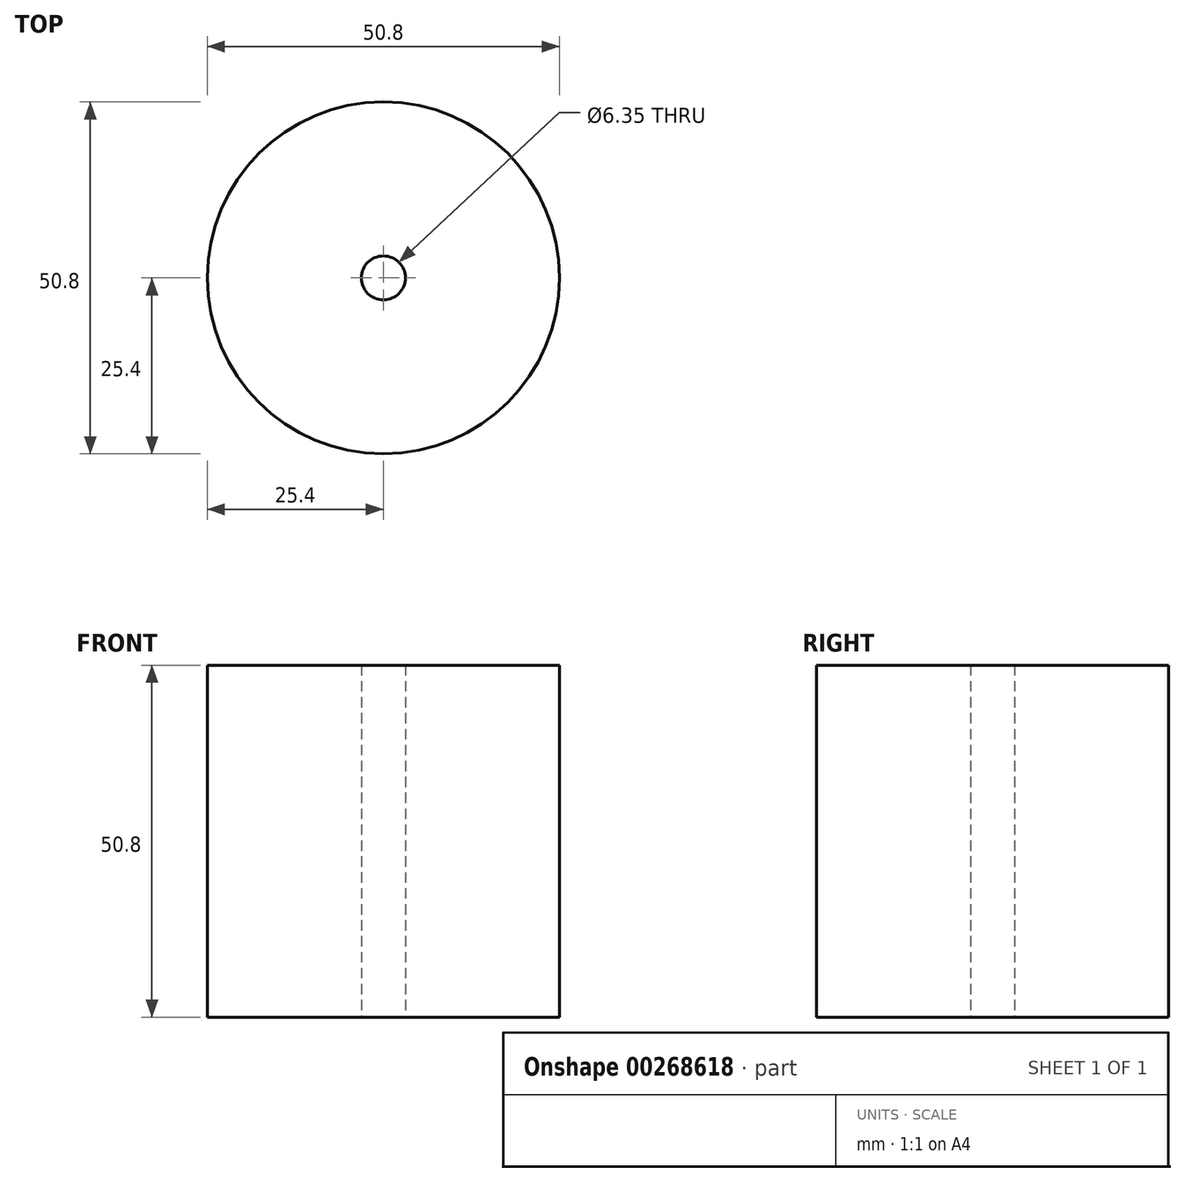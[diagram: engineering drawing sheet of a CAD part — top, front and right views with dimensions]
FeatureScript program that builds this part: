
annotation { "Feature Type Name" : "Feature", "Feature Type Description" : "" }
export const myFeature = defineFeature(function(context is Context, id is Id, definition is map)
    precondition{}
    {
        {
            var Q0;
            Q0=qCreatedBy(makeId("Top.planeOp"),FACE);
            var sketch = newSketch(context, id + "F0", { "sketchPlane" : qUnion([Q0])});
            skCircle(sketch, "E0", {"center": v(0, 0) * mm, "radius": 25.4 * mm});
            skCircle(sketch, "E1", {"center": v(0, 0) * mm, "radius": 3.17 * mm});
            skSolve(sketch);
        }
        {
            var Q0;
            Q0 = qSketchRegion(id + "F0", true);
            extrude(context, id + "F1", {"entities" : qUnion([Q0]), "depth" : 50.8 * mm});
        }
    });
